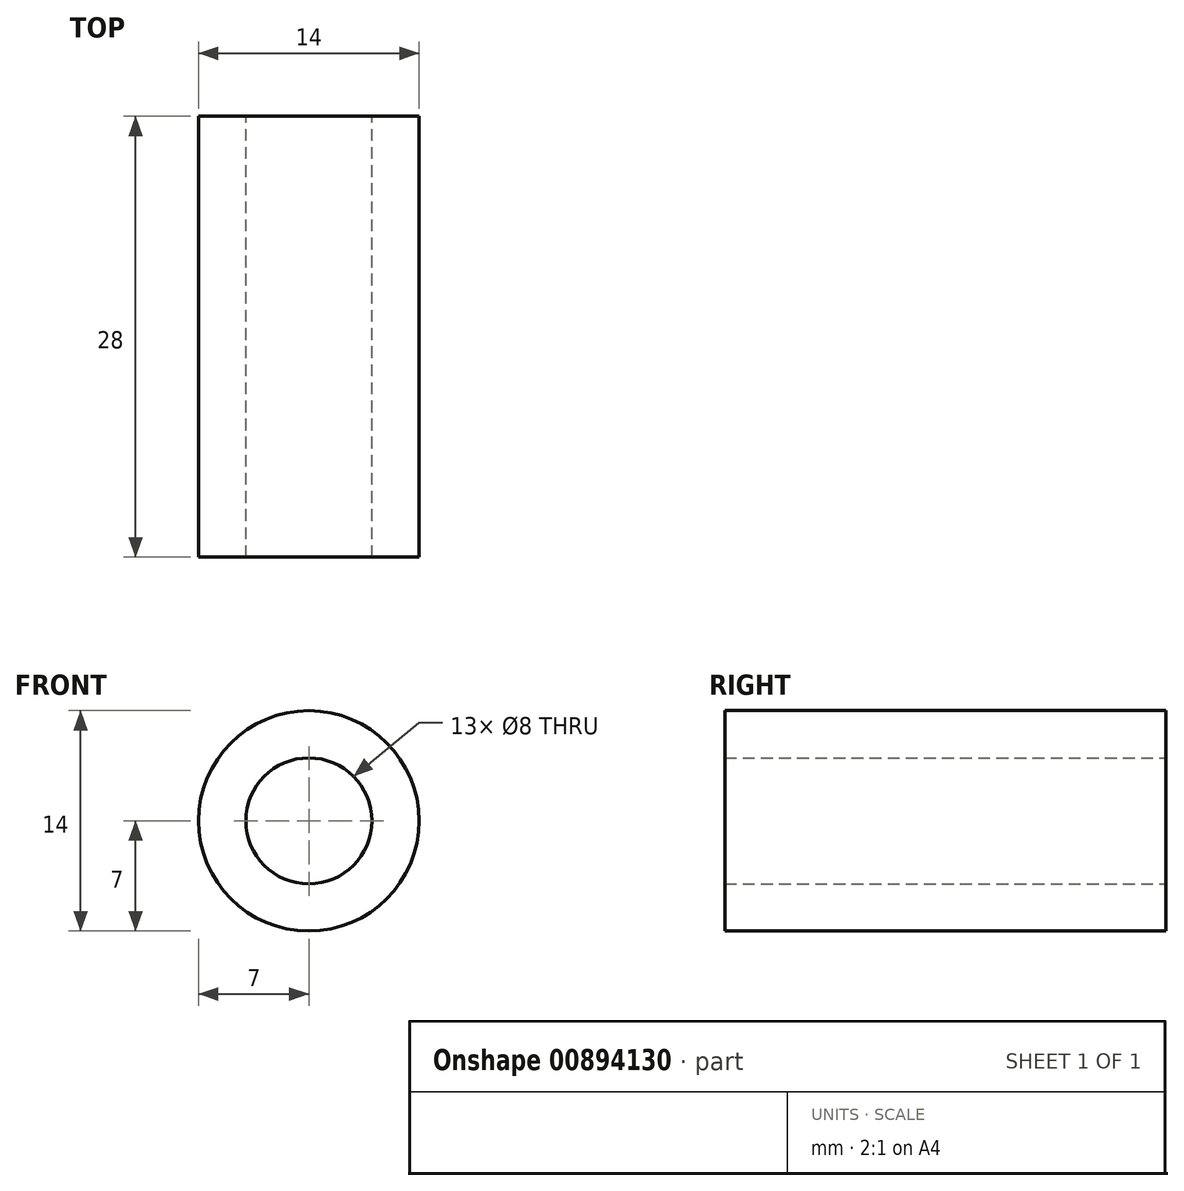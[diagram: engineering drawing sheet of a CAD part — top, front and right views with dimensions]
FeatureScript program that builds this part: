
annotation { "Feature Type Name" : "Feature", "Feature Type Description" : "" }
export const myFeature = defineFeature(function(context is Context, id is Id, definition is map)
    precondition{}
    {
        {
            var Q0;
            Q0=qCreatedBy(makeId("Front.planeOp"),FACE);
            var sketch = newSketch(context, id + "F0", { "sketchPlane" : qUnion([Q0])});
            skCircle(sketch, "E0", {"center": v(0, 0) * mm, "radius": 4 * mm});
            skCircle(sketch, "E1", {"center": v(0, 0) * mm, "radius": 7 * mm});
            skSolve(sketch);
        }
        {
            var Q0;
            Q0 = qSketchRegion(id + "F0", true);
            extrude(context, id + "F1", {"entities" : qUnion([Q0]), "depth" : 28 * mm, "offsetDistance" : 25 * mm});
        }
    });
